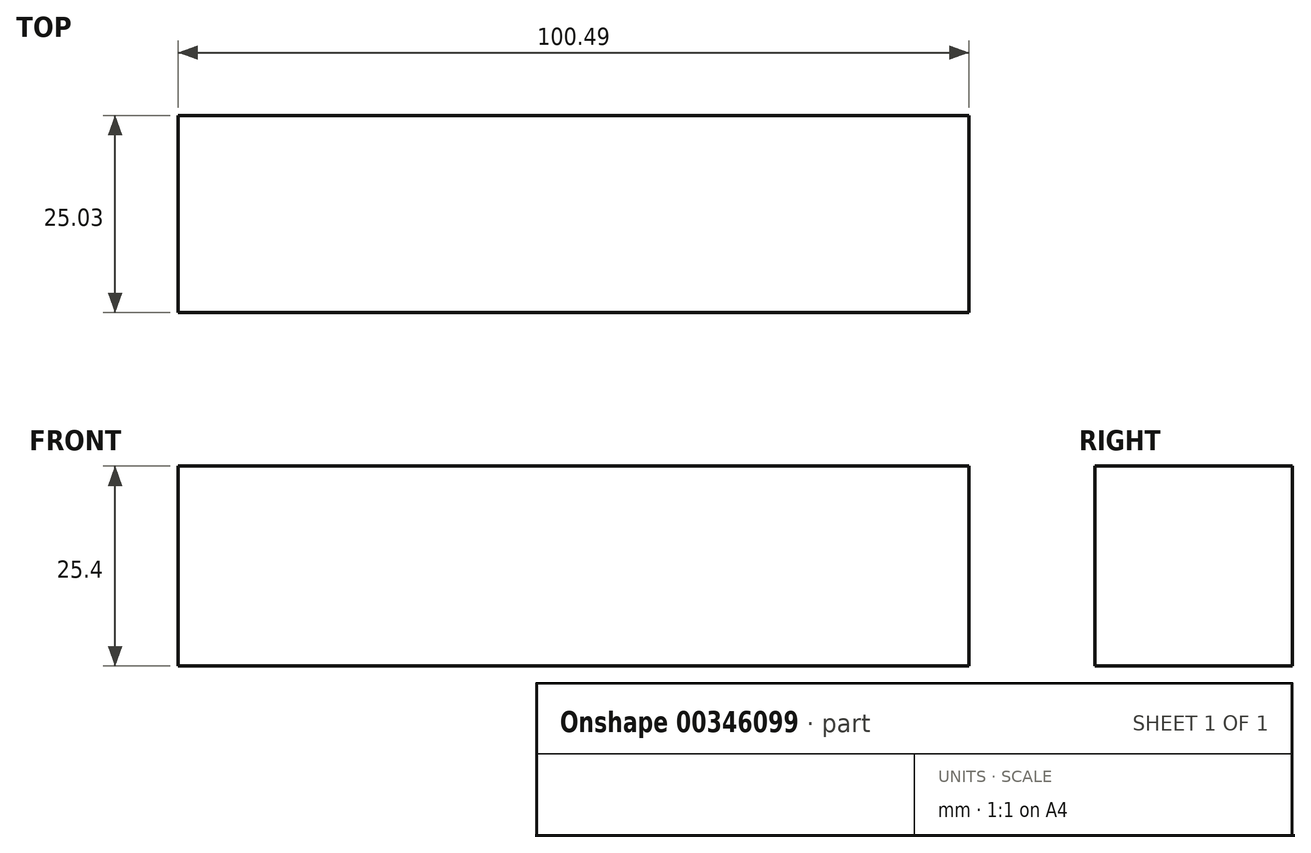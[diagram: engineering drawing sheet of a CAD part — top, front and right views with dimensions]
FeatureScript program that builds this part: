
annotation { "Feature Type Name" : "Feature", "Feature Type Description" : "" }
export const myFeature = defineFeature(function(context is Context, id is Id, definition is map)
    precondition{}
    {
        {
            var Q0;
            Q0=qCreatedBy(makeId("Top.planeOp"),FACE);
            var sketch = newSketch(context, id + "F0", { "sketchPlane" : qUnion([Q0])});
            skLineSegment(sketch, "E0.bottom", {"start": v(-69.25, -17.3) * mm, "end": v(31.24, -17.3) * mm});
            skLineSegment(sketch, "E0.top", {"start": v(-69.25, -42.32) * mm, "end": v(31.24, -42.32) * mm});
            skLineSegment(sketch, "E0.left", {"start": v(-69.25, -17.3) * mm, "end": v(-69.25, -42.32) * mm});
            skLineSegment(sketch, "E0.right", {"start": v(31.24, -17.3) * mm, "end": v(31.24, -42.32) * mm});
            skSolve(sketch);
        }
        {
            var Q0;
            Q0 = qSketchRegion(id + "F0", true);
            extrude(context, id + "F1", {"entities" : qUnion([Q0]), "depth" : 25.4 * mm});
        }
    });
